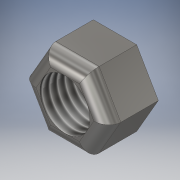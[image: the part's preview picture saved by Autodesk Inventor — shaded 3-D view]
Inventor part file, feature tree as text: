
AUTODESK INVENTOR PART (.ipt)
format: ipt  version: 2018 (Build 220112000, 112)  size: 133,120 bytes
history: native  units: in
note: dims shown in document units (in); Inventor stores cm internally (conversion verified against a paired STEP export)
features: extrude x2, sketch x2, thread x1, fillet x1
ambient origin geometry x8: Origin, YZ Plane, XZ Plane, XY Plane, X Axis, Y Axis, Z Axis, Center Point
bodies: Solid1 (feature_tree)
feature tree (6):
  extrude  "Extrusion1"  Depth=0.5in TaperAngle=0.0deg
  extrude  "Extrusion2"  Depth=0.5in TaperAngle=0.0deg
  thread  "Thread1"  [1 undecoded]
  fillet  "Fillet1"  Radius=0.125in
  sketch  "Sketch1"  dims[d0=0.75in d1=0.5in d2=0.0in]
  sketch  "Sketch2"  dims[d3=0.5in d4=0.5in d5=0.0in d6=1.0in d7=0.0in d8=0.125in]
note: 1 required parameter value undecoded (feature->parameter linkage not recoverable at this tier; creation-order binding heuristic only, values carry confidence <= 0.55)
